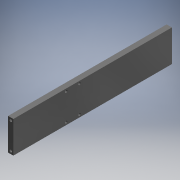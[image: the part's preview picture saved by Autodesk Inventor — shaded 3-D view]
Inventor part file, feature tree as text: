
AUTODESK INVENTOR PART (.ipt)
format: ipt  version: 2019 (Build 230136000, 136)  size: 126,464 bytes
history: native  units: mm (DEFAULTED — no unit token found)
features: extrude x3, sketch x3, plane x2, mirror x2, fillet x1
ambient origin geometry x8: Origin, YZ Plane, XZ Plane, XY Plane, X Axis, Y Axis, Z Axis, Center Point
bodies: Solid1 (feature_tree)
feature tree (11):
  extrude  "Extrusion1"  Depth=38.1mm
  extrude  "Extrusion2"  Depth=190.5mm
  plane  "Work Plane1"
  mirror  "Mirror1"
  extrude  "Extrusion3"  Depth=0.0254mm
  plane  "Work Plane2"
  mirror  "Mirror2"
  fillet  "Fillet1"  Radius=3.175mm
  sketch  "Sketch1"  dims[d0=6.35mm d1=38.1mm]
  sketch  "Sketch2"  dims[d2=190.5mm d3=0.0mm d4=3.048mm]
  sketch  "Sketch3"  dims[d5=3.048mm d6=3.175mm d7=3.175mm d8=3.175mm d9=3.175mm d10=6.35mm d11=0.0mm d12=3.048mm d13=3.048mm d14=16.002mm d15=63.5mm d16=110.998mm d17=2.921mm d18=2.921mm d19=6.35mm d20=0.0mm d21=0.0254mm]
